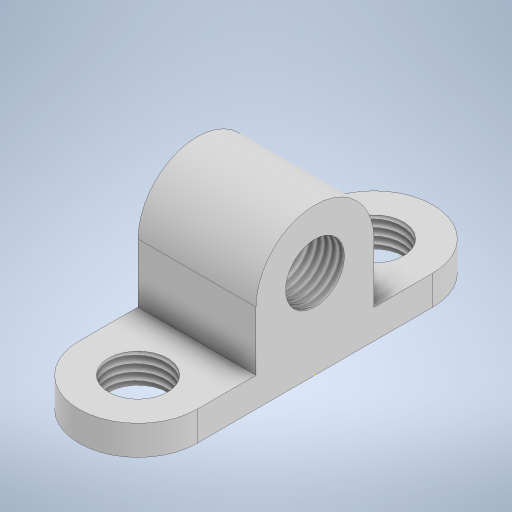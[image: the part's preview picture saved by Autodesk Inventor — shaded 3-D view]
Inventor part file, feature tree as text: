
AUTODESK INVENTOR PART (.ipt)
format: ipt  version: 2024 (Build 280153000, 153)  size: 268,800 bytes
history: native  units: mm
features: sketch x4, thread x3, extrude x2
ambient origin geometry x8: Origin, YZ Plane, XZ Plane, XY Plane, X Axis, Y Axis, Z Axis, Center Point
bodies: Solid1 (feature_tree)
feature tree (9):
  sketch  "Sketch1"  dims[d10=10.0mm d11=0.0mm d15=40.0mm d16=0.0mm]
  extrude  "Extrusion1"  Depth=40.0mm TaperAngle=0.0deg
  extrude  "Extrusion2"  Depth=10.0mm TaperAngle=0.0deg
  thread  "Thread1"  [1 undecoded]
  thread  "Thread2"  [1 undecoded]
  thread  "Thread3"  [1 undecoded]
  sketch  "Sketch4"
  sketch  "Sketch2"  dims[d17=10.0mm d18=0.0mm d19=10.0mm d20=0.0mm d21=40.0mm d22=0.0mm]
  sketch  "Sketch3"
note: 3 required parameter values undecoded (feature->parameter linkage not recoverable at this tier; creation-order binding heuristic only, values carry confidence <= 0.55)
